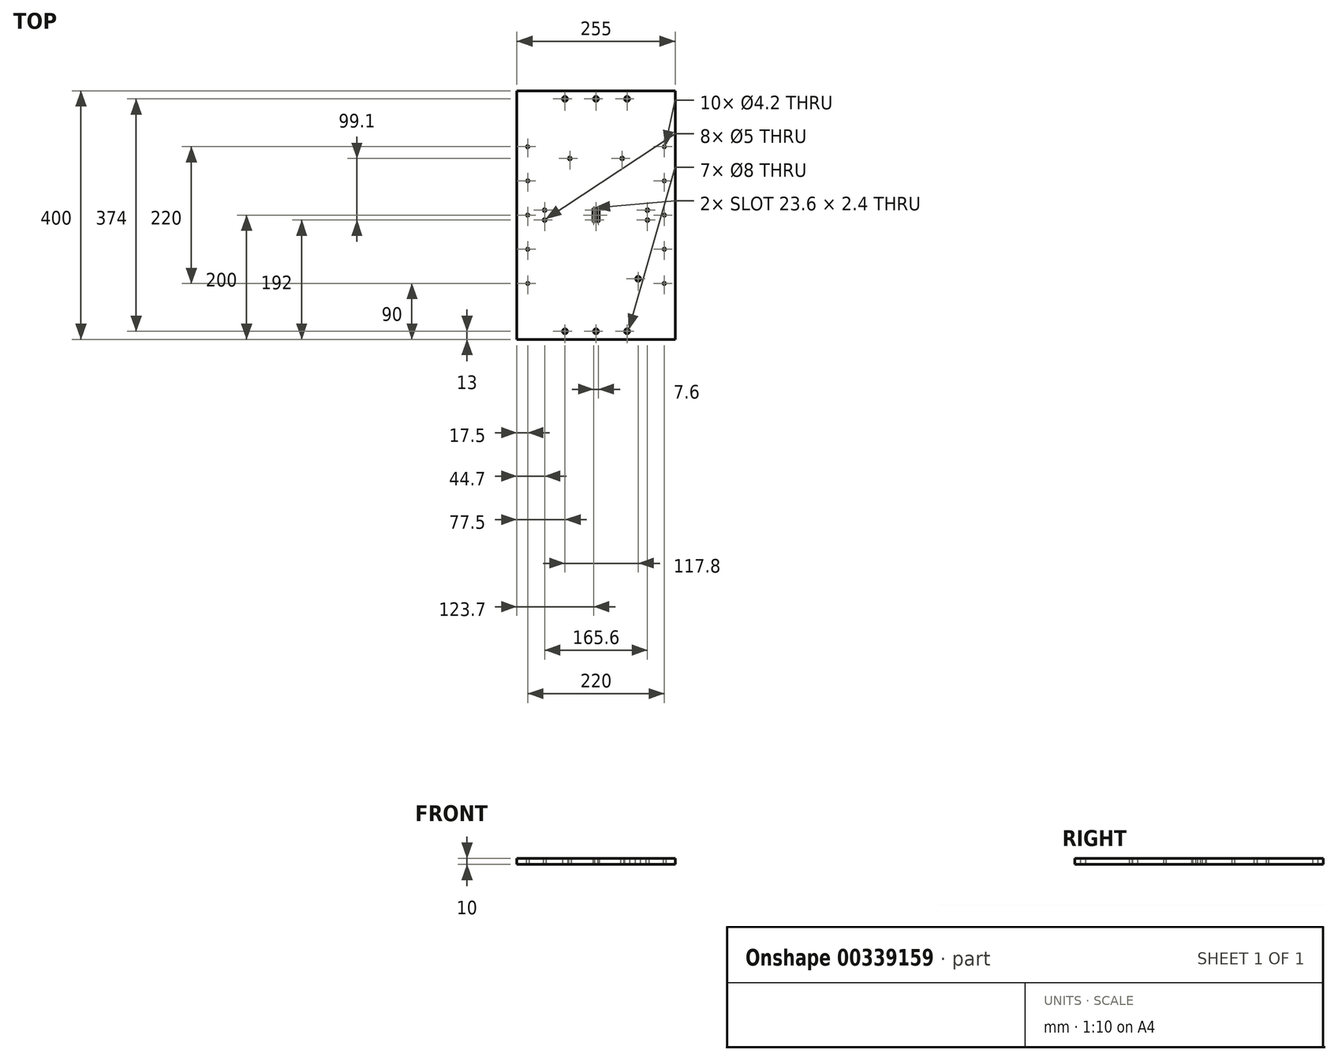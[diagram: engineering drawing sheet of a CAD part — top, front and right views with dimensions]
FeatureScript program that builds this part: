
annotation { "Feature Type Name" : "Feature", "Feature Type Description" : "" }
export const myFeature = defineFeature(function(context is Context, id is Id, definition is map)
    precondition{}
    {
        {
            var Q0;
            Q0=qCreatedBy(makeId("Top.planeOp"),FACE);
            var sketch = newSketch(context, id + "F0", { "sketchPlane" : qUnion([Q0])});
            skLineSegment(sketch, "E0.bottom", {"start": v(127.5, 200) * mm, "end": v(-127.5, 200) * mm});
            skLineSegment(sketch, "E0.top", {"start": v(127.5, -200) * mm, "end": v(-127.5, -200) * mm});
            skLineSegment(sketch, "E0.left", {"start": v(127.5, 200) * mm, "end": v(127.5, -200) * mm});
            skLineSegment(sketch, "E0.right", {"start": v(-127.5, 200) * mm, "end": v(-127.5, -200) * mm});
            skPoint(sketch, "E0.middle", {"position": v(0, 0) * mm});
            skLineSegment(sketch, "E1", {"start": v(-127.5, 0) * mm, "end": v(127.5, 0) * mm, "construction": true});
            skLineSegment(sketch, "E2", {"start": v(0, 200) * mm, "end": v(0, -200) * mm, "construction": true});
            skPoint(sketch, "E3.middle", {"position": v(-42.2, 0) * mm});
            skLineSegment(sketch, "E4.bottom", {"start": v(-2.6, 90.1) * mm, "end": v(-81.8, 90.1) * mm});
            skLineSegment(sketch, "E4.top", {"start": v(-2.6, -90.1) * mm, "end": v(-81.8, -90.1) * mm});
            skLineSegment(sketch, "E4.left", {"start": v(-2.6, 90.1) * mm, "end": v(-2.6, -90.1) * mm});
            skLineSegment(sketch, "E4.right", {"start": v(-81.8, 90.1) * mm, "end": v(-81.8, -90.1) * mm});
            skLineSegment(sketch, "E5.MirrorCS", {"start": v(2.6, 90.1) * mm, "end": v(81.8, 90.1) * mm});
            skLineSegment(sketch, "E6.MirrorCS", {"start": v(81.8, 90.1) * mm, "end": v(81.8, -90.1) * mm});
            skLineSegment(sketch, "E7.MirrorCS", {"start": v(2.6, -90.1) * mm, "end": v(81.8, -90.1) * mm});
            skLineSegment(sketch, "E8.MirrorCS", {"start": v(2.6, 90.1) * mm, "end": v(2.6, -90.1) * mm});
            skLineSegment(sketch, "E9", {"start": v(79.4, 0) * mm, "end": v(79.4, -10) * mm});
            skArc(sketch, "E10", {"start": v(79.4, -10) * mm, "mid": v(80.3, -11.3) * mm, "end": v(81.8, -11.8) * mm});
            skPoint(sketch, "E11", {"position": v(42.2, -87.6) * mm});
            skLineSegment(sketch, "E12", {"start": v(42.2, -87.6) * mm, "end": v(42.2, 87.6) * mm, "construction": true});
            skLineSegment(sketch, "E13", {"start": v(42.2, -87.6) * mm, "end": v(47.2, -87.6) * mm});
            skArc(sketch, "E14", {"start": v(49.7, -90.1) * mm, "mid": v(48.97, -88.33) * mm, "end": v(47.2, -87.6) * mm});
            skCircle(sketch, "E15", {"center": v(110, 0) * mm, "radius": 2.1 * mm});
            skCircle(sketch, "E16", {"center": v(110, -55) * mm, "radius": 2.1 * mm});
            skCircle(sketch, "E17", {"center": v(110, -110) * mm, "radius": 2.1 * mm});
            skCircle(sketch, "E18.MirrorC", {"center": v(110, 55) * mm, "radius": 2.1 * mm});
            skCircle(sketch, "E19.MirrorC", {"center": v(110, 110) * mm, "radius": 2.1 * mm});
            skCircle(sketch, "E20.MirrorC", {"center": v(-110, 0) * mm, "radius": 2.1 * mm});
            skCircle(sketch, "E21.MirrorC", {"center": v(-110, -110) * mm, "radius": 2.1 * mm});
            skCircle(sketch, "E22.MirrorC", {"center": v(-110, -55) * mm, "radius": 2.1 * mm});
            skCircle(sketch, "E23.MirrorC", {"center": v(-110, 55) * mm, "radius": 2.1 * mm});
            skCircle(sketch, "E24.MirrorC", {"center": v(-110, 110) * mm, "radius": 2.1 * mm});
            skArc(sketch, "E25.MirrorCS", {"start": v(79.4, 10) * mm, "mid": v(80.3, 11.3) * mm, "end": v(81.8, 11.8) * mm});
            skLineSegment(sketch, "E26.MirrorCS", {"start": v(79.4, 0) * mm, "end": v(79.4, 10) * mm});
            skPoint(sketch, "E27.MirrorP", {"position": v(42.2, 87.6) * mm});
            skLineSegment(sketch, "E28.MirrorCS", {"start": v(42.2, 87.6) * mm, "end": v(47.2, 87.6) * mm});
            skArc(sketch, "E29.MirrorCS", {"start": v(49.7, 90.1) * mm, "mid": v(48.97, 88.33) * mm, "end": v(47.2, 87.6) * mm});
            skLineSegment(sketch, "E30.MirrorCS", {"start": v(42.2, 87.6) * mm, "end": v(37.2, 87.6) * mm});
            skArc(sketch, "E31.MirrorCS", {"start": v(5, -10) * mm, "mid": v(4.1, -11.3) * mm, "end": v(2.6, -11.8) * mm});
            skLineSegment(sketch, "E32.MirrorCS", {"start": v(42.2, -87.6) * mm, "end": v(37.2, -87.6) * mm});
            skArc(sketch, "E33.MirrorCS", {"start": v(34.7, 90.1) * mm, "mid": v(35.43, 88.33) * mm, "end": v(37.2, 87.6) * mm});
            skArc(sketch, "E34.MirrorCS", {"start": v(34.7, -90.1) * mm, "mid": v(35.43, -88.33) * mm, "end": v(37.2, -87.6) * mm});
            skArc(sketch, "E35.MirrorCS", {"start": v(5, 10) * mm, "mid": v(4.1, 11.3) * mm, "end": v(2.6, 11.8) * mm});
            skLineSegment(sketch, "E36.MirrorCS", {"start": v(5, 0) * mm, "end": v(5, -10) * mm});
            skLineSegment(sketch, "E37.MirrorCS", {"start": v(5, 0) * mm, "end": v(5, 10) * mm});
            skLineSegment(sketch, "E38.MirrorCS", {"start": v(-42.2, 87.6) * mm, "end": v(-37.2, 87.6) * mm});
            skArc(sketch, "E39.MirrorCS", {"start": v(-49.7, 90.1) * mm, "mid": v(-48.97, 88.33) * mm, "end": v(-47.2, 87.6) * mm});
            skLineSegment(sketch, "E40.MirrorCS", {"start": v(-42.2, 87.6) * mm, "end": v(-47.2, 87.6) * mm});
            skArc(sketch, "E41.MirrorCS", {"start": v(-34.7, 90.1) * mm, "mid": v(-35.43, 88.33) * mm, "end": v(-37.2, 87.6) * mm});
            skPoint(sketch, "E42.MirrorP", {"position": v(-42.2, 87.6) * mm});
            skArc(sketch, "E43.MirrorCS", {"start": v(-5, 10) * mm, "mid": v(-4.1, 11.3) * mm, "end": v(-2.6, 11.8) * mm});
            skArc(sketch, "E44.MirrorCS", {"start": v(-5, -10) * mm, "mid": v(-4.1, -11.3) * mm, "end": v(-2.6, -11.8) * mm});
            skLineSegment(sketch, "E45.MirrorCS", {"start": v(-5, 0) * mm, "end": v(-5, 10) * mm});
            skLineSegment(sketch, "E46.MirrorCS", {"start": v(-5, 0) * mm, "end": v(-5, -10) * mm});
            skLineSegment(sketch, "E47.MirrorCS", {"start": v(-79.4, 0) * mm, "end": v(-79.4, 10) * mm});
            skArc(sketch, "E48.MirrorCS", {"start": v(-79.4, 10) * mm, "mid": v(-80.3, 11.3) * mm, "end": v(-81.8, 11.8) * mm});
            skLineSegment(sketch, "E49.MirrorCS", {"start": v(-79.4, 0) * mm, "end": v(-79.4, -10) * mm});
            skArc(sketch, "E50.MirrorCS", {"start": v(-79.4, -10) * mm, "mid": v(-80.3, -11.3) * mm, "end": v(-81.8, -11.8) * mm});
            skPoint(sketch, "E51.MirrorP", {"position": v(-42.2, -87.6) * mm});
            skLineSegment(sketch, "E52.MirrorCS", {"start": v(-42.2, -87.6) * mm, "end": v(-47.2, -87.6) * mm});
            skArc(sketch, "E53.MirrorCS", {"start": v(-34.7, -90.1) * mm, "mid": v(-35.43, -88.33) * mm, "end": v(-37.2, -87.6) * mm});
            skLineSegment(sketch, "E54.MirrorCS", {"start": v(-42.2, -87.6) * mm, "end": v(-37.2, -87.6) * mm});
            skArc(sketch, "E55.MirrorCS", {"start": v(-49.7, -90.1) * mm, "mid": v(-48.97, -88.33) * mm, "end": v(-47.2, -87.6) * mm});
            skCircle(sketch, "E56", {"center": v(42.2, 91.1) * mm, "radius": 2.5 * mm});
            skPoint(sketch, "E56.centerSnap0", {"position": v(42.2, 90.1) * mm});
            skCircle(sketch, "E57", {"center": v(82.8, 8) * mm, "radius": 2.5 * mm});
            skCircle(sketch, "E58.MirrorC", {"center": v(82.8, -8) * mm, "radius": 2.5 * mm});
            skCircle(sketch, "E59.MirrorC", {"center": v(-82.8, 8) * mm, "radius": 2.5 * mm});
            skCircle(sketch, "E60.MirrorC", {"center": v(-82.8, -8) * mm, "radius": 2.5 * mm});
            skCircle(sketch, "E61.MirrorC", {"center": v(-42.2, 91.1) * mm, "radius": 2.5 * mm});
            skCircle(sketch, "E62", {"center": v(0, 8) * mm, "radius": 2.5 * mm});
            skCircle(sketch, "E63.MirrorC", {"center": v(0, -8) * mm, "radius": 2.5 * mm});
            skCircle(sketch, "E64", {"center": v(0, 187) * mm, "radius": 4 * mm});
            skCircle(sketch, "E65", {"center": v(50, 187) * mm, "radius": 4 * mm});
            skCircle(sketch, "E66", {"center": v(-50, 187) * mm, "radius": 4 * mm});
            skCircle(sketch, "E67.MirrorC", {"center": v(0, -187) * mm, "radius": 4 * mm});
            skCircle(sketch, "E68.MirrorC", {"center": v(-50, -187) * mm, "radius": 4 * mm});
            skCircle(sketch, "E69.MirrorC", {"center": v(50, -187) * mm, "radius": 4 * mm});
            skSolve(sketch);
        }
        {
            var Q0;
            Q0=makeQuery(id+"F0.imprint","IMPRINT",FACE,{"disambiguationData":[TD([[makeQuery(id+"F0.imprint","IMPRINT",EDGE,{"derivedFrom":sQuery(id+"F0.wireOp",EDGE,"E0.bottom")}),1.0]])]});
            var Q1;
            Q1=makeQuery(id+"F0.imprint","IMPRINT",FACE,{"disambiguationData":[TD([[makeQuery(id+"F0.imprint","IMPRINT",EDGE,{"derivedFrom":sQuery(id+"F0.wireOp",EDGE,"E9")}),1.0]])]});
            var Q2;
            Q2=makeQuery(id+"F0.imprint","IMPRINT",FACE,{"disambiguationData":[TD([[makeQuery(id+"F0.imprint","IMPRINT",EDGE,{"derivedFrom":sQuery(id+"F0.wireOp",EDGE,"E28.MirrorCS")}),1.0]])]});
            var Q3;
            Q3=makeQuery(id+"F0.imprint","IMPRINT",FACE,{"disambiguationData":[TD([[makeQuery(id+"F0.imprint","IMPRINT",EDGE,{"derivedFrom":sQuery(id+"F0.wireOp",EDGE,"E13")}),-1.0]])]});
            var Q4;
            {var subQ1=sQuery(id+"F0.wireOp",EDGE,"E31.MirrorCS");Q4=makeQuery(id+"F0.imprint","IMPRINT",FACE,{"disambiguationData":[TD([[makeQuery(id+"F0.imprint","IMPRINT",EDGE,{"derivedFrom":subQ1}),-1.0]])]});}
            var Q5;
            {var subQ1=sQuery(id+"F0.wireOp",EDGE,"E43.MirrorCS");Q5=makeQuery(id+"F0.imprint","IMPRINT",FACE,{"disambiguationData":[TD([[makeQuery(id+"F0.imprint","IMPRINT",EDGE,{"derivedFrom":subQ1}),-1.0]])]});}
            var Q6;
            Q6=makeQuery(id+"F0.imprint","IMPRINT",FACE,{"disambiguationData":[TD([[makeQuery(id+"F0.imprint","IMPRINT",EDGE,{"derivedFrom":sQuery(id+"F0.wireOp",EDGE,"E47.MirrorCS")}),1.0]])]});
            var Q7;
            Q7=makeQuery(id+"F0.imprint","IMPRINT",FACE,{"disambiguationData":[TD([[makeQuery(id+"F0.imprint","IMPRINT",EDGE,{"derivedFrom":sQuery(id+"F0.wireOp",EDGE,"E38.MirrorCS")}),1.0]])]});
            var Q8;
            Q8=makeQuery(id+"F0.imprint","IMPRINT",FACE,{"disambiguationData":[TD([[makeQuery(id+"F0.imprint","IMPRINT",EDGE,{"derivedFrom":sQuery(id+"F0.wireOp",EDGE,"E52.MirrorCS")}),1.0]])]});
            extrude(context, id + "F1", {"entities" : qUnion([Q0, Q1, Q2, Q3, Q4, Q5, Q6, Q7, Q8]), "depth" : 10 * mm});
        }
        {
            var Q0;
            Q0=makeQuery(id+"F1.opExtrude","CAP_FACE",FACE,{"disambiguationData":[OSD([sQuery(id+"F0.wireOp",EDGE,"E0.bottom"),sQuery(id+"F0.wireOp",EDGE,"E0.top"),sQuery(id+"F0.wireOp",EDGE,"E0.left"),sQuery(id+"F0.wireOp",EDGE,"E0.right"),sQuery(id+"F0.wireOp",EDGE,"E4.top"),sQuery(id+"F0.wireOp",EDGE,"E4.left"),sQuery(id+"F0.wireOp",EDGE,"E4.right"),sQuery(id+"F0.wireOp",EDGE,"E5.MirrorCS"),sQuery(id+"F0.wireOp",EDGE,"E6.MirrorCS"),sQuery(id+"F0.wireOp",EDGE,"E7.MirrorCS"),sQuery(id+"F0.wireOp",EDGE,"E9"),sQuery(id+"F0.wireOp",EDGE,"E10"),sQuery(id+"F0.wireOp",EDGE,"E13"),sQuery(id+"F0.wireOp",EDGE,"E14"),sQuery(id+"F0.wireOp",EDGE,"E16"),sQuery(id+"F0.wireOp",EDGE,"E17"),sQuery(id+"F0.wireOp",EDGE,"E18.MirrorC"),sQuery(id+"F0.wireOp",EDGE,"E15"),sQuery(id+"F0.wireOp",EDGE,"E19.MirrorC"),sQuery(id+"F0.wireOp",EDGE,"E20.MirrorC"),sQuery(id+"F0.wireOp",EDGE,"E21.MirrorC"),sQuery(id+"F0.wireOp",EDGE,"E22.MirrorC"),sQuery(id+"F0.wireOp",EDGE,"E23.MirrorC"),sQuery(id+"F0.wireOp",EDGE,"E24.MirrorC"),sQuery(id+"F0.wireOp",EDGE,"E25.MirrorCS"),sQuery(id+"F0.wireOp",EDGE,"E26.MirrorCS"),sQuery(id+"F0.wireOp",EDGE,"E28.MirrorCS"),sQuery(id+"F0.wireOp",EDGE,"E29.MirrorCS"),sQuery(id+"F0.wireOp",EDGE,"E30.MirrorCS"),sQuery(id+"F0.wireOp",EDGE,"E31.MirrorCS"),sQuery(id+"F0.wireOp",EDGE,"E32.MirrorCS"),sQuery(id+"F0.wireOp",EDGE,"E33.MirrorCS"),sQuery(id+"F0.wireOp",EDGE,"E34.MirrorCS"),sQuery(id+"F0.wireOp",EDGE,"E35.MirrorCS"),sQuery(id+"F0.wireOp",EDGE,"E8.MirrorCS"),sQuery(id+"F0.wireOp",EDGE,"E36.MirrorCS"),sQuery(id+"F0.wireOp",EDGE,"E37.MirrorCS"),sQuery(id+"F0.wireOp",EDGE,"E38.MirrorCS"),sQuery(id+"F0.wireOp",EDGE,"E39.MirrorCS"),sQuery(id+"F0.wireOp",EDGE,"E40.MirrorCS"),sQuery(id+"F0.wireOp",EDGE,"E41.MirrorCS"),sQuery(id+"F0.wireOp",EDGE,"E43.MirrorCS"),sQuery(id+"F0.wireOp",EDGE,"E44.MirrorCS"),sQuery(id+"F0.wireOp",EDGE,"E45.MirrorCS"),sQuery(id+"F0.wireOp",EDGE,"E46.MirrorCS"),sQuery(id+"F0.wireOp",EDGE,"E47.MirrorCS"),sQuery(id+"F0.wireOp",EDGE,"E48.MirrorCS"),sQuery(id+"F0.wireOp",EDGE,"E49.MirrorCS"),sQuery(id+"F0.wireOp",EDGE,"E50.MirrorCS"),sQuery(id+"F0.wireOp",EDGE,"E52.MirrorCS"),sQuery(id+"F0.wireOp",EDGE,"E53.MirrorCS"),sQuery(id+"F0.wireOp",EDGE,"E54.MirrorCS"),sQuery(id+"F0.wireOp",EDGE,"E55.MirrorCS"),sQuery(id+"F0.wireOp",EDGE,"E56"),sQuery(id+"F0.wireOp",EDGE,"E57"),sQuery(id+"F0.wireOp",EDGE,"E58.MirrorC"),sQuery(id+"F0.wireOp",EDGE,"E59.MirrorC"),sQuery(id+"F0.wireOp",EDGE,"E60.MirrorC"),sQuery(id+"F0.wireOp",EDGE,"E4.bottom"),sQuery(id+"F0.wireOp",EDGE,"E61.MirrorC"),sQuery(id+"F0.wireOp",EDGE,"E62"),sQuery(id+"F0.wireOp",EDGE,"E63.MirrorC"),sQuery(id+"F0.wireOp",EDGE,"E64"),sQuery(id+"F0.wireOp",EDGE,"E65"),sQuery(id+"F0.wireOp",EDGE,"E66"),sQuery(id+"F0.wireOp",EDGE,"E67.MirrorC"),sQuery(id+"F0.wireOp",EDGE,"E68.MirrorC"),sQuery(id+"F0.wireOp",EDGE,"E69.MirrorC")])],"isStart":false});
            var sketch = newSketch(context, id + "F2", { "sketchPlane" : qUnion([Q0])});
            skLineSegment(sketch, "E70", {"start": v(-42.2, -87.6) * mm, "end": v(-42.2, -102.6) * mm, "construction": true});
            skPoint(sketch, "E70.endSnap0", {"position": v(-42.2, -87.6) * mm});
            skLineSegment(sketch, "E71", {"start": v(-42.2, -102.6) * mm, "end": v(67.8, -102.6) * mm, "construction": true});
            skCircle(sketch, "E72", {"center": v(67.8, -102.6) * mm, "radius": 4 * mm});
            skSolve(sketch);
        }
        {
            var Q0;
            Q0=makeQuery(id+"F2.imprint","IMPRINT",FACE,{"disambiguationData":[TD([[makeQuery(id+"F2.imprint","IMPRINT",EDGE,{"derivedFrom":sQuery(id+"F2.wireOp",EDGE,"E72")}),1.0]])]});
            extrude(context, id + "F3", {"entities" : qUnion([Q0]), "operationType" : NewBodyOperationType.REMOVE, "endBound" : BoundingType.THROUGH_ALL, "oppositeDirection" : true, "depth" : 25 * mm});
        }
    });
